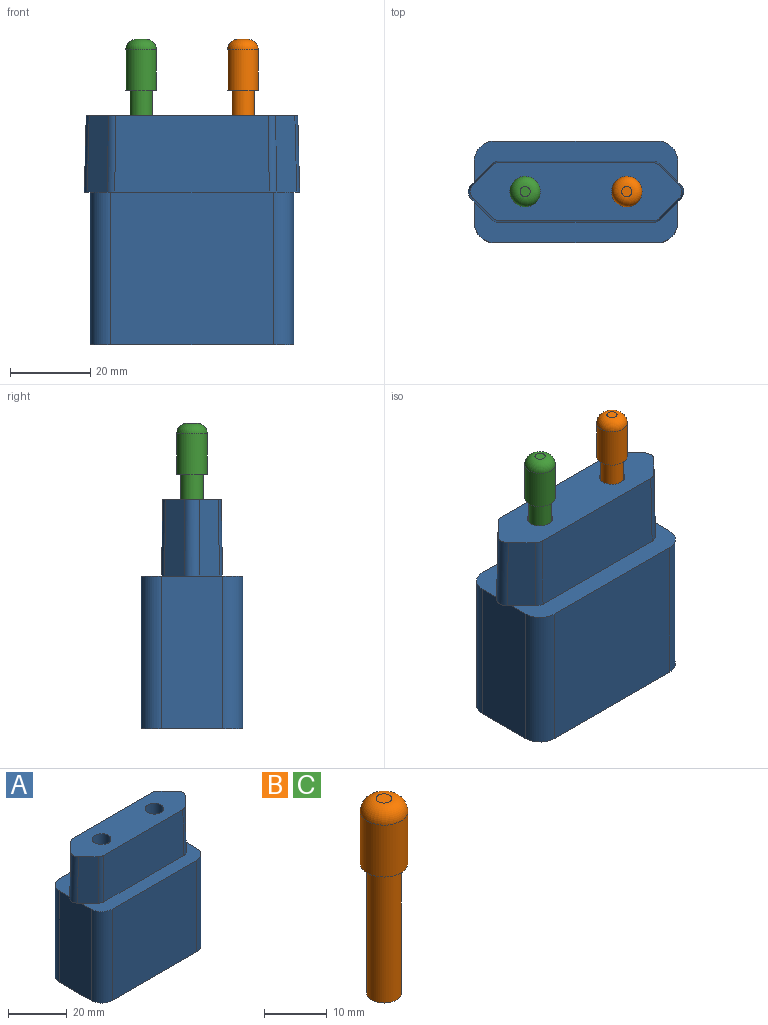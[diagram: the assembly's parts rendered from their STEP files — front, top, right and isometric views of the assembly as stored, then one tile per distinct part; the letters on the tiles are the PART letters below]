
ASSEMBLY  parts=3 mates=2
PART A: 40 faces, bbox 53.8x25.4x57.2 mm
  f0: plane 50.8x25.4mm, normal (0,0,-1), area 1113.3mm2, adj f3,f4,f5,f6,f7,f8,f9,f10
  f1: plane 50.81x10.17mm, normal (0,0,1), area 273.1mm2, adj f3,f5,f6,f9,f10,f12,f16,f17
  f2: plane 50.81x10.17mm, normal (0,0,1), area 273.1mm2, adj f3,f4,f5,f7,f8,f13,f14,f15
  f3: plane 38.1x15.24mm, normal (-1,0,0), area 580.6mm2, adj f0,f1,f2,f7,f10,f19
  f4: plane 40.64x38.1mm, normal (0,-1,0), area 1548.4mm2, adj f0,f2,f7,f8
  f5: plane 38.1x15.24mm, normal (1,0,0), area 580.6mm2, adj f0,f1,f2,f8,f9,f11
  f6: plane 40.64x38.1mm, normal (0,1,0), area 1548.4mm2, adj f0,f1,f9,f10
  f7: cylinder r=5.08mm len=38.1mm, axis (0,0,1), area 304mm2, adj f0,f2,f3,f4
  f8: cylinder r=5.08mm len=38.1mm, axis (0,0,-1), area 304mm2, adj f0,f2,f4,f5
  f9: cylinder r=5.08mm len=38.1mm, axis (0,0,1), area 304mm2, adj f0,f1,f5,f6
  f10: cylinder r=5.08mm len=38.1mm, axis (0,0,-1), area 304mm2, adj f0,f1,f3,f6
  f11: plane 5.08x1.49mm, normal (0,0,-1), area 5.1mm2, adj f5,f15,f16,f21
  f12: plane 19.05x5.22mm, normal (-0.71,0.71,0.02), area 132.4mm2, adj f1,f18,f19,f20,f25
  f13: plane 19.05x5.22mm, normal (-0.71,-0.71,0.02), area 132.4mm2, adj f2,f18,f19,f20,f22
  f14: plane 38.54x19.05mm, normal (0,-1,0.02), area 731.6mm2, adj f2,f18,f22,f23
  f15: plane 19.05x5.22mm, normal (0.71,-0.71,0.02), area 132.4mm2, adj f2,f11,f18,f21,f23
  f16: plane 19.05x5.22mm, normal (0.71,0.71,0.02), area 132.4mm2, adj f1,f11,f18,f21,f24
  f17: plane 38.54x19.05mm, normal (0,1,0.02), area 731.6mm2, adj f1,f18,f24,f25
  f18: plane 52.84x14.58mm, normal (0,0,1), area 627.9mm2, adj f12,f13,f14,f15,f16,f17,f20,f21
  f19: plane 5.08x1.49mm, normal (0,0,-1), area 5.1mm2, adj f3,f12,f13,f20
  f20: cylinder r=2.54mm len=19.09mm, axis (-0.02,0,-1), area 76mm2, adj f12,f13,f18,f19
  f21: cylinder r=2.54mm len=19.09mm, axis (0.02,0,-1), area 76mm2, adj f11,f15,f16,f18
  f22: cylinder r=2.54mm len=19.05mm, axis (-0.01,-0.02,-1), area 38mm2, adj f2,f13,f14,f18
  f23: cylinder r=2.54mm len=19.05mm, axis (0.01,-0.02,-1), area 38mm2, adj f2,f14,f15,f18
  f24: cylinder r=2.54mm len=19.05mm, axis (0.01,0.02,-1), area 38mm2, adj f1,f16,f17,f18
  f25: cylinder r=2.54mm len=19.05mm, axis (-0.01,0.02,-1), area 38mm2, adj f1,f12,f17,f18
  f26: plane 6.35x6.35mm, normal (0,0,1), area 31.7mm2, adj f27
  f27: cylinder r=3.17mm len=19.05mm, axis (0,0,1), area 380mm2, adj f18,f26
  f28: plane 6.35x6.35mm, normal (0,0,1), area 31.7mm2, adj f29
  f29: cylinder r=3.17mm len=19.05mm, axis (0,0,1), area 380mm2, adj f18,f28
  f30: plane 15.24x12.7mm, normal (0,1,0), area 193.5mm2, adj f0,f31,f33,f34
  f31: plane 12.7x5.08mm, normal (1,0,0), area 64.5mm2, adj f0,f30,f32,f34
  f32: plane 15.24x12.7mm, normal (0,-1,0), area 193.5mm2, adj f0,f31,f33,f34
  f33: plane 12.7x5.08mm, normal (-1,0,0), area 64.5mm2, adj f0,f30,f32,f34
  f34: plane 15.24x5.08mm, normal (0,0,-1), area 77.4mm2, adj f30,f31,f32,f33
  f35: plane 12.7x5.08mm, normal (1,0,0), area 64.5mm2, adj f0,f36,f38,f39
  f36: plane 15.24x12.7mm, normal (0,-1,0), area 193.5mm2, adj f0,f35,f37,f39
  f37: plane 12.7x5.08mm, normal (-1,0,0), area 64.5mm2, adj f0,f36,f38,f39
  f38: plane 15.24x12.7mm, normal (0,1,0), area 193.5mm2, adj f0,f35,f37,f39
  f39: plane 15.24x5.08mm, normal (0,0,-1), area 77.4mm2, adj f35,f36,f37,f38
PART B: 6 faces, bbox 7.6x7.6x38.1 mm
  f0: cylinder r=2.79mm len=25.4mm, axis (0,0,-1), area 445.9mm2, adj f1,f3
  f1: plane 5.59x5.59mm, normal (0,0,-1), area 24.5mm2, adj f0
  f2: cylinder r=3.81mm len=10.16mm, axis (0,0,1), area 243.2mm2, adj f3,f5
  f3: plane 7.62x7.62mm, normal (0,0,-1), area 21.1mm2, adj f0,f2
  f4: plane 2.54x2.54mm, normal (0,0,1), area 5.1mm2, adj f5
  f5: torus R=1.27mm, axis (0,0,1), area 72.4mm2, adj f2,f4
PART C: same geometry as B
PLACE A t=(-14.35,6.6,-6.24)mm
PLACE B t=(-1.65,6.6,31.86)mm
PLACE C t=(-27.05,6.6,31.86)mm
MATE fastened C.f0 <-> A.f29  axis (0,0,-1) through (-27.05,6.6,31.86)mm
MATE fastened B.f0 <-> A.f27  axis (0,0,-1) through (-1.65,6.6,31.86)mm
